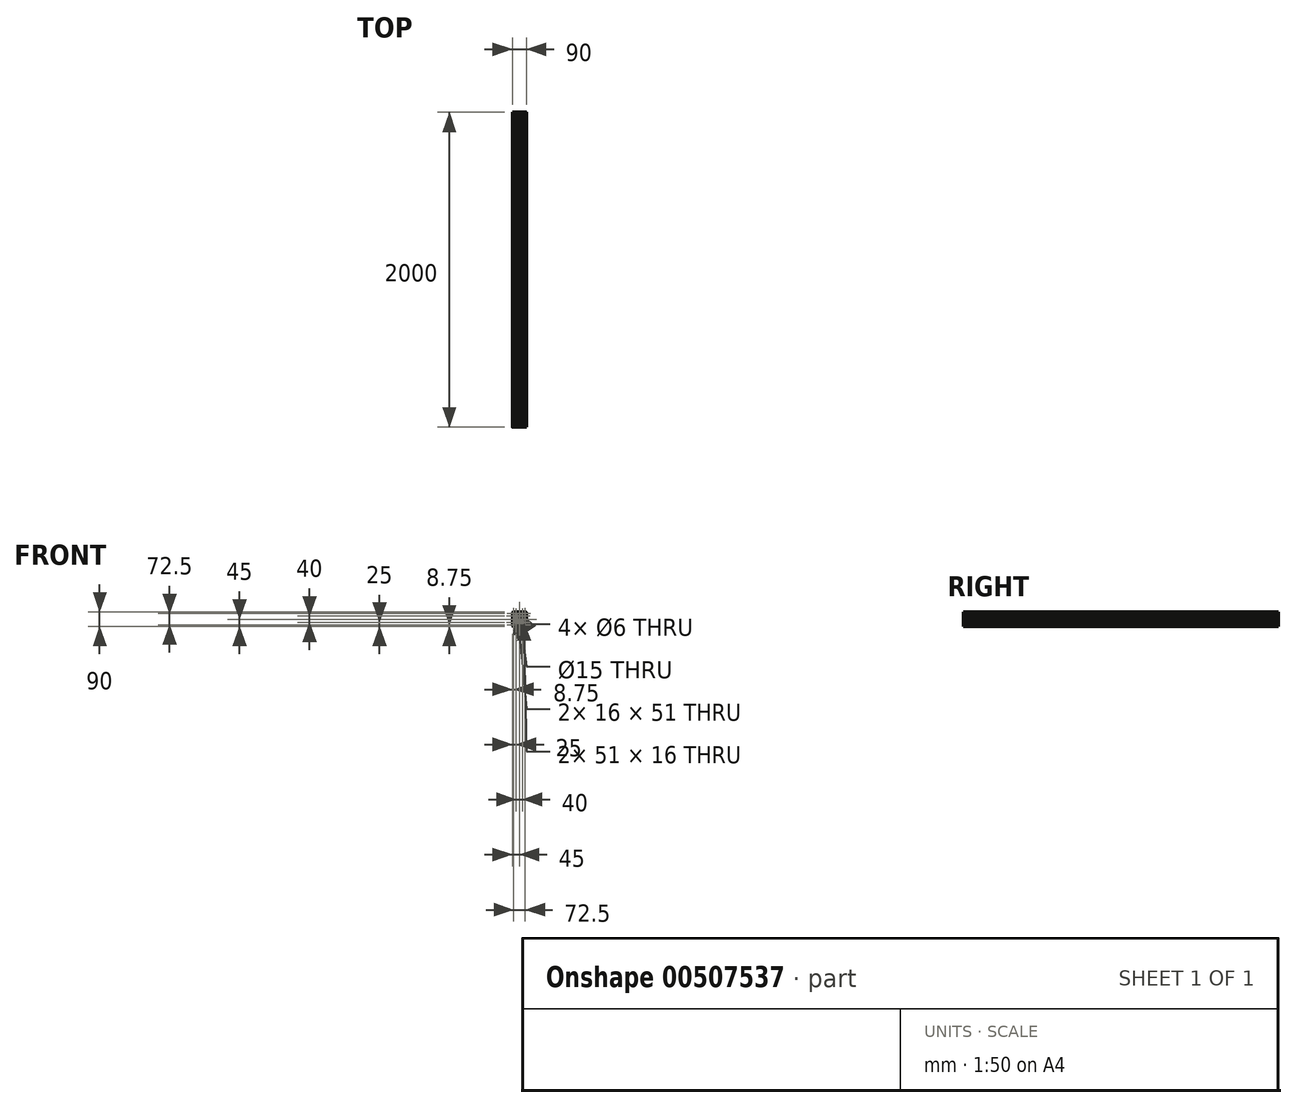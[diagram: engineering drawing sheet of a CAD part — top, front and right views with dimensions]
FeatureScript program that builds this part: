
annotation { "Feature Type Name" : "Feature", "Feature Type Description" : "" }
export const myFeature = defineFeature(function(context is Context, id is Id, definition is map)
    precondition{}
    {
        {
            var Q0;
            Q0=qCreatedBy(makeId("Front.planeOp"),FACE);
            var sketch = newSketch(context, id + "F0", { "sketchPlane" : qUnion([Q0])});
            skLineSegment(sketch, "E0", {"start": v(28, 45) * mm, "end": v(28, 44.5) * mm});
            skLineSegment(sketch, "E1", {"start": v(28, 44.5) * mm, "end": v(27.5, 44.5) * mm});
            skLineSegment(sketch, "E2", {"start": v(27.5, 44.5) * mm, "end": v(27.5, 39) * mm});
            skLineSegment(sketch, "E3", {"start": v(27.5, 39) * mm, "end": v(33.5, 39) * mm});
            skLineSegment(sketch, "E4", {"start": v(33.5, 39) * mm, "end": v(33.5, 36) * mm});
            skLineSegment(sketch, "E5", {"start": v(33.5, 36) * mm, "end": v(29.5, 32) * mm});
            skLineSegment(sketch, "E6", {"start": v(29.5, 32) * mm, "end": v(12.5, 32) * mm});
            skLineSegment(sketch, "E7", {"start": v(12.5, 32) * mm, "end": v(12.5, 39) * mm});
            skLineSegment(sketch, "E8", {"start": v(12.5, 39) * mm, "end": v(17.5, 39) * mm});
            skLineSegment(sketch, "E9", {"start": v(17.5, 39) * mm, "end": v(17.5, 44.5) * mm});
            skLineSegment(sketch, "E10", {"start": v(17.5, 44.5) * mm, "end": v(17, 44.5) * mm});
            skLineSegment(sketch, "E11", {"start": v(17, 44.5) * mm, "end": v(17, 45) * mm});
            skLineSegment(sketch, "E12", {"start": v(45, 28) * mm, "end": v(44.5, 28) * mm});
            skLineSegment(sketch, "E13", {"start": v(44.5, 28) * mm, "end": v(44.5, 27.5) * mm});
            skLineSegment(sketch, "E14", {"start": v(44.5, 27.5) * mm, "end": v(39, 27.5) * mm});
            skLineSegment(sketch, "E15", {"start": v(39, 27.5) * mm, "end": v(39, 33.5) * mm});
            skLineSegment(sketch, "E16", {"start": v(39, 33.5) * mm, "end": v(36, 33.5) * mm});
            skLineSegment(sketch, "E17", {"start": v(36, 33.5) * mm, "end": v(32, 29.5) * mm});
            skLineSegment(sketch, "E18", {"start": v(32, 29.5) * mm, "end": v(32, 12.5) * mm});
            skLineSegment(sketch, "E19", {"start": v(32, 12.5) * mm, "end": v(39, 12.5) * mm});
            skLineSegment(sketch, "E20", {"start": v(39, 12.5) * mm, "end": v(39, 17.5) * mm});
            skLineSegment(sketch, "E21", {"start": v(39, 17.5) * mm, "end": v(44.5, 17.5) * mm});
            skLineSegment(sketch, "E22", {"start": v(44.5, 17.5) * mm, "end": v(44.5, 17) * mm});
            skLineSegment(sketch, "E23", {"start": v(44.5, 17) * mm, "end": v(45, 17) * mm});
            skLineSegment(sketch, "E24", {"start": v(45, 28) * mm, "end": v(45, 40) * mm});
            skLineSegment(sketch, "E25", {"start": v(28, 45) * mm, "end": v(40, 45) * mm});
            skPoint(sketch, "E26.visualSharp", {"position": v(45, 45) * mm});
            skArc(sketch, "E26.filletArc", {"start": v(45, 40) * mm, "mid": v(43.54, 43.54) * mm, "end": v(40, 45) * mm});
            skLineSegment(sketch, "E27", {"start": v(17, 45) * mm, "end": v(9.5, 45) * mm});
            skLineSegment(sketch, "E28", {"start": v(9.5, 45) * mm, "end": v(9.5, 44.5) * mm});
            skLineSegment(sketch, "E29", {"start": v(9.5, 44.5) * mm, "end": v(0, 44.5) * mm});
            skLineSegment(sketch, "E30", {"start": v(0, 44.5) * mm, "end": v(0, 39.25) * mm});
            skLineSegment(sketch, "E31", {"start": v(45, 17) * mm, "end": v(45, 9.5) * mm});
            skLineSegment(sketch, "E32", {"start": v(45, 9.5) * mm, "end": v(44.5, 9.5) * mm});
            skLineSegment(sketch, "E33", {"start": v(44.5, 9.5) * mm, "end": v(44.5, 0) * mm});
            skLineSegment(sketch, "E34", {"start": v(44.5, 0) * mm, "end": v(39.25, 0) * mm});
            skLineSegment(sketch, "E35.bottom", {"start": v(7.5, 0) * mm, "end": v(12, 0) * mm});
            skLineSegment(sketch, "E35.top", {"start": v(0, 28) * mm, "end": v(25.5, 28) * mm});
            skLineSegment(sketch, "E35.right", {"start": v(28, 0) * mm, "end": v(28, 25.5) * mm});
            skLineSegment(sketch, "E36.top", {"start": v(0, 12) * mm, "end": v(9.5, 12) * mm});
            skLineSegment(sketch, "E36.left", {"start": v(0, 7.5) * mm, "end": v(0, 12) * mm});
            skLineSegment(sketch, "E36.right", {"start": v(12, 0) * mm, "end": v(12, 9.5) * mm});
            skArc(sketch, "E37", {"start": v(7.5, 0) * mm, "mid": v(5.3, 5.3) * mm, "end": v(0, 7.5) * mm});
            skLineSegment(sketch, "E38", {"start": v(25.5, 28) * mm, "end": v(9.5, 12) * mm});
            skLineSegment(sketch, "E39", {"start": v(28, 25.5) * mm, "end": v(12, 9.5) * mm});
            skLineSegment(sketch, "E40.trimOffspring", {"start": v(12, 0) * mm, "end": v(7.5, 0) * mm});
            skLineSegment(sketch, "E41.trimOffspring", {"start": v(0, 12) * mm, "end": v(0, 7.5) * mm});
            skArc(sketch, "E42", {"start": v(39.25, 0) * mm, "mid": v(36.25, 3) * mm, "end": v(33.25, 0) * mm});
            skArc(sketch, "E43", {"start": v(0, 33.25) * mm, "mid": v(3, 36.25) * mm, "end": v(0, 39.25) * mm});
            skLineSegment(sketch, "E44.trimOffspring", {"start": v(0, 33.25) * mm, "end": v(0, 28) * mm});
            skLineSegment(sketch, "E45.trimOffspring", {"start": v(33.25, 0) * mm, "end": v(28, 0) * mm});
            skLineSegment(sketch, "E46.1.0", {"start": v(-28, 0) * mm, "end": v(-28, 25.5) * mm});
            skLineSegment(sketch, "E46.1.1", {"start": v(0, 28) * mm, "end": v(-25.5, 28) * mm});
            skPoint(sketch, "E46.1.2", {"position": v(-45, 45) * mm});
            skArc(sketch, "E46.1.3", {"start": v(0, 39.25) * mm, "mid": v(-3, 36.25) * mm, "end": v(0, 33.25) * mm});
            skLineSegment(sketch, "E46.1.4", {"start": v(-25.5, 28) * mm, "end": v(-9.5, 12) * mm});
            skLineSegment(sketch, "E46.1.5", {"start": v(-44.5, 9.5) * mm, "end": v(-44.5, 0) * mm});
            skLineSegment(sketch, "E46.1.6", {"start": v(-28, 25.5) * mm, "end": v(-12, 9.5) * mm});
            skLineSegment(sketch, "E46.1.7", {"start": v(-28, 45) * mm, "end": v(-40, 45) * mm});
            skLineSegment(sketch, "E46.1.8", {"start": v(-32, 29.5) * mm, "end": v(-32, 12.5) * mm});
            skArc(sketch, "E46.1.9", {"start": v(-33.25, 0) * mm, "mid": v(-36.25, 3) * mm, "end": v(-39.25, 0) * mm});
            skLineSegment(sketch, "E46.1.10", {"start": v(-9.5, 44.5) * mm, "end": v(0, 44.5) * mm});
            skLineSegment(sketch, "E46.1.11", {"start": v(-12.5, 32) * mm, "end": v(-12.5, 39) * mm});
            skLineSegment(sketch, "E46.1.12", {"start": v(-12, 0) * mm, "end": v(-12, 9.5) * mm});
            skLineSegment(sketch, "E46.1.13", {"start": v(-45, 17) * mm, "end": v(-45, 9.5) * mm});
            skArc(sketch, "E46.1.14", {"start": v(-40, 45) * mm, "mid": v(-43.54, 43.54) * mm, "end": v(-45, 40) * mm});
            skArc(sketch, "E46.1.15", {"start": v(0, 7.5) * mm, "mid": v(-5.3, 5.3) * mm, "end": v(-7.5, 0) * mm});
            skLineSegment(sketch, "E46.1.16", {"start": v(-45, 28) * mm, "end": v(-45, 40) * mm});
            skLineSegment(sketch, "E46.1.17", {"start": v(0, 12) * mm, "end": v(-9.5, 12) * mm});
            skLineSegment(sketch, "E46.1.18", {"start": v(-17, 45) * mm, "end": v(-9.5, 45) * mm});
            skLineSegment(sketch, "E46.1.19", {"start": v(-32, 12.5) * mm, "end": v(-39, 12.5) * mm});
            skLineSegment(sketch, "E46.1.20", {"start": v(-29.5, 32) * mm, "end": v(-12.5, 32) * mm});
            skLineSegment(sketch, "E46.1.21", {"start": v(-12.5, 39) * mm, "end": v(-17.5, 39) * mm});
            skLineSegment(sketch, "E46.1.22", {"start": v(-17.5, 39) * mm, "end": v(-17.5, 44.5) * mm});
            skLineSegment(sketch, "E46.1.23", {"start": v(-44.5, 0) * mm, "end": v(-39.25, 0) * mm});
            skLineSegment(sketch, "E46.1.24", {"start": v(-27.5, 39) * mm, "end": v(-33.5, 39) * mm});
            skLineSegment(sketch, "E46.1.25", {"start": v(-36, 33.5) * mm, "end": v(-32, 29.5) * mm});
            skLineSegment(sketch, "E46.1.26", {"start": v(-39, 12.5) * mm, "end": v(-39, 17.5) * mm});
            skLineSegment(sketch, "E46.1.27", {"start": v(-39, 17.5) * mm, "end": v(-44.5, 17.5) * mm});
            skLineSegment(sketch, "E46.1.28", {"start": v(-33.5, 39) * mm, "end": v(-33.5, 36) * mm});
            skLineSegment(sketch, "E46.1.29", {"start": v(-33.5, 36) * mm, "end": v(-29.5, 32) * mm});
            skLineSegment(sketch, "E46.1.30", {"start": v(-33.25, 0) * mm, "end": v(-28, 0) * mm});
            skLineSegment(sketch, "E46.1.33", {"start": v(-12, 0) * mm, "end": v(-7.5, 0) * mm});
            skLineSegment(sketch, "E46.1.34", {"start": v(-27.5, 44.5) * mm, "end": v(-27.5, 39) * mm});
            skLineSegment(sketch, "E46.1.35", {"start": v(-44.5, 27.5) * mm, "end": v(-39, 27.5) * mm});
            skLineSegment(sketch, "E46.1.36", {"start": v(-39, 27.5) * mm, "end": v(-39, 33.5) * mm});
            skLineSegment(sketch, "E46.1.37", {"start": v(-39, 33.5) * mm, "end": v(-36, 33.5) * mm});
            skLineSegment(sketch, "E46.1.39", {"start": v(-7.5, 0) * mm, "end": v(-12, 0) * mm});
            skLineSegment(sketch, "E46.1.40", {"start": v(-45, 28) * mm, "end": v(-44.5, 28) * mm});
            skLineSegment(sketch, "E46.1.41", {"start": v(-44.5, 28) * mm, "end": v(-44.5, 27.5) * mm});
            skLineSegment(sketch, "E46.1.42", {"start": v(-9.5, 45) * mm, "end": v(-9.5, 44.5) * mm});
            skLineSegment(sketch, "E46.1.43", {"start": v(-17.5, 44.5) * mm, "end": v(-17, 44.5) * mm});
            skLineSegment(sketch, "E46.1.45", {"start": v(-17, 44.5) * mm, "end": v(-17, 45) * mm});
            skLineSegment(sketch, "E46.1.46", {"start": v(-45, 9.5) * mm, "end": v(-44.5, 9.5) * mm});
            skLineSegment(sketch, "E46.1.47", {"start": v(-44.5, 17) * mm, "end": v(-45, 17) * mm});
            skLineSegment(sketch, "E46.1.49", {"start": v(-44.5, 17.5) * mm, "end": v(-44.5, 17) * mm});
            skLineSegment(sketch, "E46.1.50", {"start": v(-28, 44.5) * mm, "end": v(-27.5, 44.5) * mm});
            skLineSegment(sketch, "E46.1.51", {"start": v(-28, 45) * mm, "end": v(-28, 44.5) * mm});
            skLineSegment(sketch, "E46.2.0", {"start": v(0, -28) * mm, "end": v(-25.5, -28) * mm});
            skLineSegment(sketch, "E46.2.1", {"start": v(-28, 0) * mm, "end": v(-28, -25.5) * mm});
            skPoint(sketch, "E46.2.2", {"position": v(-45, -45) * mm});
            skArc(sketch, "E46.2.3", {"start": v(-39.25, 0) * mm, "mid": v(-36.25, -3) * mm, "end": v(-33.25, 0) * mm});
            skLineSegment(sketch, "E46.2.4", {"start": v(-28, -25.5) * mm, "end": v(-12, -9.5) * mm});
            skLineSegment(sketch, "E46.2.5", {"start": v(-9.5, -44.5) * mm, "end": v(0, -44.5) * mm});
            skLineSegment(sketch, "E46.2.6", {"start": v(-25.5, -28) * mm, "end": v(-9.5, -12) * mm});
            skLineSegment(sketch, "E46.2.7", {"start": v(-45, -28) * mm, "end": v(-45, -40) * mm});
            skLineSegment(sketch, "E46.2.8", {"start": v(-29.5, -32) * mm, "end": v(-12.5, -32) * mm});
            skArc(sketch, "E46.2.9", {"start": v(0, -33.25) * mm, "mid": v(-3, -36.25) * mm, "end": v(0, -39.25) * mm});
            skLineSegment(sketch, "E46.2.10", {"start": v(-44.5, -9.5) * mm, "end": v(-44.5, 0) * mm});
            skLineSegment(sketch, "E46.2.11", {"start": v(-32, -12.5) * mm, "end": v(-39, -12.5) * mm});
            skLineSegment(sketch, "E46.2.12", {"start": v(0, -12) * mm, "end": v(-9.5, -12) * mm});
            skLineSegment(sketch, "E46.2.13", {"start": v(-17, -45) * mm, "end": v(-9.5, -45) * mm});
            skArc(sketch, "E46.2.14", {"start": v(-45, -40) * mm, "mid": v(-43.54, -43.54) * mm, "end": v(-40, -45) * mm});
            skArc(sketch, "E46.2.15", {"start": v(-7.5, 0) * mm, "mid": v(-5.3, -5.3) * mm, "end": v(0, -7.5) * mm});
            skLineSegment(sketch, "E46.2.16", {"start": v(-28, -45) * mm, "end": v(-40, -45) * mm});
            skLineSegment(sketch, "E46.2.17", {"start": v(-12, 0) * mm, "end": v(-12, -9.5) * mm});
            skLineSegment(sketch, "E46.2.18", {"start": v(-45, -17) * mm, "end": v(-45, -9.5) * mm});
            skLineSegment(sketch, "E46.2.19", {"start": v(-12.5, -32) * mm, "end": v(-12.5, -39) * mm});
            skLineSegment(sketch, "E46.2.20", {"start": v(-32, -29.5) * mm, "end": v(-32, -12.5) * mm});
            skLineSegment(sketch, "E46.2.21", {"start": v(-39, -12.5) * mm, "end": v(-39, -17.5) * mm});
            skLineSegment(sketch, "E46.2.22", {"start": v(-39, -17.5) * mm, "end": v(-44.5, -17.5) * mm});
            skLineSegment(sketch, "E46.2.23", {"start": v(0, -44.5) * mm, "end": v(0, -39.25) * mm});
            skLineSegment(sketch, "E46.2.24", {"start": v(-39, -27.5) * mm, "end": v(-39, -33.5) * mm});
            skLineSegment(sketch, "E46.2.25", {"start": v(-33.5, -36) * mm, "end": v(-29.5, -32) * mm});
            skLineSegment(sketch, "E46.2.26", {"start": v(-12.5, -39) * mm, "end": v(-17.5, -39) * mm});
            skLineSegment(sketch, "E46.2.27", {"start": v(-17.5, -39) * mm, "end": v(-17.5, -44.5) * mm});
            skLineSegment(sketch, "E46.2.28", {"start": v(-39, -33.5) * mm, "end": v(-36, -33.5) * mm});
            skLineSegment(sketch, "E46.2.29", {"start": v(-36, -33.5) * mm, "end": v(-32, -29.5) * mm});
            skLineSegment(sketch, "E46.2.30", {"start": v(0, -33.25) * mm, "end": v(0, -28) * mm});
            skLineSegment(sketch, "E46.2.31", {"start": v(-33.25, 0) * mm, "end": v(-28, 0) * mm});
            skLineSegment(sketch, "E46.2.32", {"start": v(-44.5, 0) * mm, "end": v(-39.25, 0) * mm});
            skLineSegment(sketch, "E46.2.33", {"start": v(0, -12) * mm, "end": v(0, -7.5) * mm});
            skLineSegment(sketch, "E46.2.34", {"start": v(-44.5, -27.5) * mm, "end": v(-39, -27.5) * mm});
            skLineSegment(sketch, "E46.2.35", {"start": v(-27.5, -44.5) * mm, "end": v(-27.5, -39) * mm});
            skLineSegment(sketch, "E46.2.36", {"start": v(-27.5, -39) * mm, "end": v(-33.5, -39) * mm});
            skLineSegment(sketch, "E46.2.37", {"start": v(-33.5, -39) * mm, "end": v(-33.5, -36) * mm});
            skLineSegment(sketch, "E46.2.38", {"start": v(-12, 0) * mm, "end": v(-7.5, 0) * mm});
            skLineSegment(sketch, "E46.2.39", {"start": v(0, -7.5) * mm, "end": v(0, -12) * mm});
            skLineSegment(sketch, "E46.2.40", {"start": v(-28, -45) * mm, "end": v(-28, -44.5) * mm});
            skLineSegment(sketch, "E46.2.41", {"start": v(-28, -44.5) * mm, "end": v(-27.5, -44.5) * mm});
            skLineSegment(sketch, "E46.2.42", {"start": v(-45, -9.5) * mm, "end": v(-44.5, -9.5) * mm});
            skLineSegment(sketch, "E46.2.43", {"start": v(-44.5, -17.5) * mm, "end": v(-44.5, -17) * mm});
            skLineSegment(sketch, "E46.2.44", {"start": v(-7.5, 0) * mm, "end": v(-12, 0) * mm});
            skLineSegment(sketch, "E46.2.45", {"start": v(-44.5, -17) * mm, "end": v(-45, -17) * mm});
            skLineSegment(sketch, "E46.2.46", {"start": v(-9.5, -45) * mm, "end": v(-9.5, -44.5) * mm});
            skLineSegment(sketch, "E46.2.47", {"start": v(-17, -44.5) * mm, "end": v(-17, -45) * mm});
            skLineSegment(sketch, "E46.2.48", {"start": v(-7.5, 0) * mm, "end": v(-12, 0) * mm});
            skLineSegment(sketch, "E46.2.49", {"start": v(-17.5, -44.5) * mm, "end": v(-17, -44.5) * mm});
            skLineSegment(sketch, "E46.2.50", {"start": v(-44.5, -28) * mm, "end": v(-44.5, -27.5) * mm});
            skLineSegment(sketch, "E46.2.51", {"start": v(-45, -28) * mm, "end": v(-44.5, -28) * mm});
            skLineSegment(sketch, "E46.3.0", {"start": v(28, 0) * mm, "end": v(28, -25.5) * mm});
            skLineSegment(sketch, "E46.3.1", {"start": v(0, -28) * mm, "end": v(25.5, -28) * mm});
            skPoint(sketch, "E46.3.2", {"position": v(45, -45) * mm});
            skArc(sketch, "E46.3.3", {"start": v(0, -39.25) * mm, "mid": v(3, -36.25) * mm, "end": v(0, -33.25) * mm});
            skLineSegment(sketch, "E46.3.4", {"start": v(25.5, -28) * mm, "end": v(9.5, -12) * mm});
            skLineSegment(sketch, "E46.3.5", {"start": v(44.5, -9.5) * mm, "end": v(44.5, 0) * mm});
            skLineSegment(sketch, "E46.3.6", {"start": v(28, -25.5) * mm, "end": v(12, -9.5) * mm});
            skLineSegment(sketch, "E46.3.7", {"start": v(28, -45) * mm, "end": v(40, -45) * mm});
            skLineSegment(sketch, "E46.3.8", {"start": v(32, -29.5) * mm, "end": v(32, -12.5) * mm});
            skArc(sketch, "E46.3.9", {"start": v(33.25, 0) * mm, "mid": v(36.25, -3) * mm, "end": v(39.25, 0) * mm});
            skLineSegment(sketch, "E46.3.10", {"start": v(9.5, -44.5) * mm, "end": v(0, -44.5) * mm});
            skLineSegment(sketch, "E46.3.11", {"start": v(12.5, -32) * mm, "end": v(12.5, -39) * mm});
            skLineSegment(sketch, "E46.3.12", {"start": v(12, 0) * mm, "end": v(12, -9.5) * mm});
            skLineSegment(sketch, "E46.3.13", {"start": v(45, -17) * mm, "end": v(45, -9.5) * mm});
            skArc(sketch, "E46.3.14", {"start": v(40, -45) * mm, "mid": v(43.54, -43.54) * mm, "end": v(45, -40) * mm});
            skArc(sketch, "E46.3.15", {"start": v(0, -7.5) * mm, "mid": v(5.3, -5.3) * mm, "end": v(7.5, 0) * mm});
            skLineSegment(sketch, "E46.3.16", {"start": v(45, -28) * mm, "end": v(45, -40) * mm});
            skLineSegment(sketch, "E46.3.17", {"start": v(0, -12) * mm, "end": v(9.5, -12) * mm});
            skLineSegment(sketch, "E46.3.18", {"start": v(17, -45) * mm, "end": v(9.5, -45) * mm});
            skLineSegment(sketch, "E46.3.19", {"start": v(32, -12.5) * mm, "end": v(39, -12.5) * mm});
            skLineSegment(sketch, "E46.3.20", {"start": v(29.5, -32) * mm, "end": v(12.5, -32) * mm});
            skLineSegment(sketch, "E46.3.21", {"start": v(12.5, -39) * mm, "end": v(17.5, -39) * mm});
            skLineSegment(sketch, "E46.3.22", {"start": v(17.5, -39) * mm, "end": v(17.5, -44.5) * mm});
            skLineSegment(sketch, "E46.3.24", {"start": v(27.5, -39) * mm, "end": v(33.5, -39) * mm});
            skLineSegment(sketch, "E46.3.25", {"start": v(36, -33.5) * mm, "end": v(32, -29.5) * mm});
            skLineSegment(sketch, "E46.3.26", {"start": v(39, -12.5) * mm, "end": v(39, -17.5) * mm});
            skLineSegment(sketch, "E46.3.27", {"start": v(39, -17.5) * mm, "end": v(44.5, -17.5) * mm});
            skLineSegment(sketch, "E46.3.28", {"start": v(33.5, -39) * mm, "end": v(33.5, -36) * mm});
            skLineSegment(sketch, "E46.3.29", {"start": v(33.5, -36) * mm, "end": v(29.5, -32) * mm});
            skLineSegment(sketch, "E46.3.31", {"start": v(0, -33.25) * mm, "end": v(0, -28) * mm});
            skLineSegment(sketch, "E46.3.32", {"start": v(0, -44.5) * mm, "end": v(0, -39.25) * mm});
            skLineSegment(sketch, "E46.3.34", {"start": v(27.5, -44.5) * mm, "end": v(27.5, -39) * mm});
            skLineSegment(sketch, "E46.3.35", {"start": v(44.5, -27.5) * mm, "end": v(39, -27.5) * mm});
            skLineSegment(sketch, "E46.3.36", {"start": v(39, -27.5) * mm, "end": v(39, -33.5) * mm});
            skLineSegment(sketch, "E46.3.37", {"start": v(39, -33.5) * mm, "end": v(36, -33.5) * mm});
            skLineSegment(sketch, "E46.3.38", {"start": v(0, -12) * mm, "end": v(0, -7.5) * mm});
            skLineSegment(sketch, "E46.3.40", {"start": v(45, -28) * mm, "end": v(44.5, -28) * mm});
            skLineSegment(sketch, "E46.3.41", {"start": v(44.5, -28) * mm, "end": v(44.5, -27.5) * mm});
            skLineSegment(sketch, "E46.3.42", {"start": v(9.5, -45) * mm, "end": v(9.5, -44.5) * mm});
            skLineSegment(sketch, "E46.3.43", {"start": v(17.5, -44.5) * mm, "end": v(17, -44.5) * mm});
            skLineSegment(sketch, "E46.3.44", {"start": v(0, -7.5) * mm, "end": v(0, -12) * mm});
            skLineSegment(sketch, "E46.3.45", {"start": v(17, -44.5) * mm, "end": v(17, -45) * mm});
            skLineSegment(sketch, "E46.3.46", {"start": v(45, -9.5) * mm, "end": v(44.5, -9.5) * mm});
            skLineSegment(sketch, "E46.3.47", {"start": v(44.5, -17) * mm, "end": v(45, -17) * mm});
            skLineSegment(sketch, "E46.3.48", {"start": v(0, -7.5) * mm, "end": v(0, -12) * mm});
            skLineSegment(sketch, "E46.3.49", {"start": v(44.5, -17.5) * mm, "end": v(44.5, -17) * mm});
            skLineSegment(sketch, "E46.3.50", {"start": v(28, -44.5) * mm, "end": v(27.5, -44.5) * mm});
            skLineSegment(sketch, "E46.3.51", {"start": v(28, -45) * mm, "end": v(28, -44.5) * mm});
            skPoint(sketch, "E46.center", {"position": v(0, 0) * mm});
            skSolve(sketch);
        }
        {
            var Q0;
            Q0=makeQuery(id+"F0.imprint","IMPRINT",FACE,{"disambiguationData":[TD([[makeQuery(id+"F0.imprint","IMPRINT",EDGE,{"derivedFrom":sQuery(id+"F0.wireOp",EDGE,"E46.2.0")}),1.0]])]});
            var Q1;
            Q1=makeQuery(id+"F0.imprint","IMPRINT",FACE,{"disambiguationData":[TD([[makeQuery(id+"F0.imprint","IMPRINT",EDGE,{"derivedFrom":sQuery(id+"F0.wireOp",EDGE,"E46.1.0")}),1.0]])]});
            var Q2;
            Q2=makeQuery(id+"F0.imprint","IMPRINT",FACE,{"disambiguationData":[TD([[makeQuery(id+"F0.imprint","IMPRINT",EDGE,{"derivedFrom":sQuery(id+"F0.wireOp",EDGE,"E0")}),1.0]])]});
            var Q3;
            Q3=makeQuery(id+"F0.imprint","IMPRINT",FACE,{"disambiguationData":[TD([[makeQuery(id+"F0.imprint","IMPRINT",EDGE,{"derivedFrom":sQuery(id+"F0.wireOp",EDGE,"E46.3.0")}),1.0]])]});
            extrude(context, id + "F1", {"entities" : qUnion([Q0, Q1, Q2, Q3]), "depth" : 2000 * mm});
        }
    });
